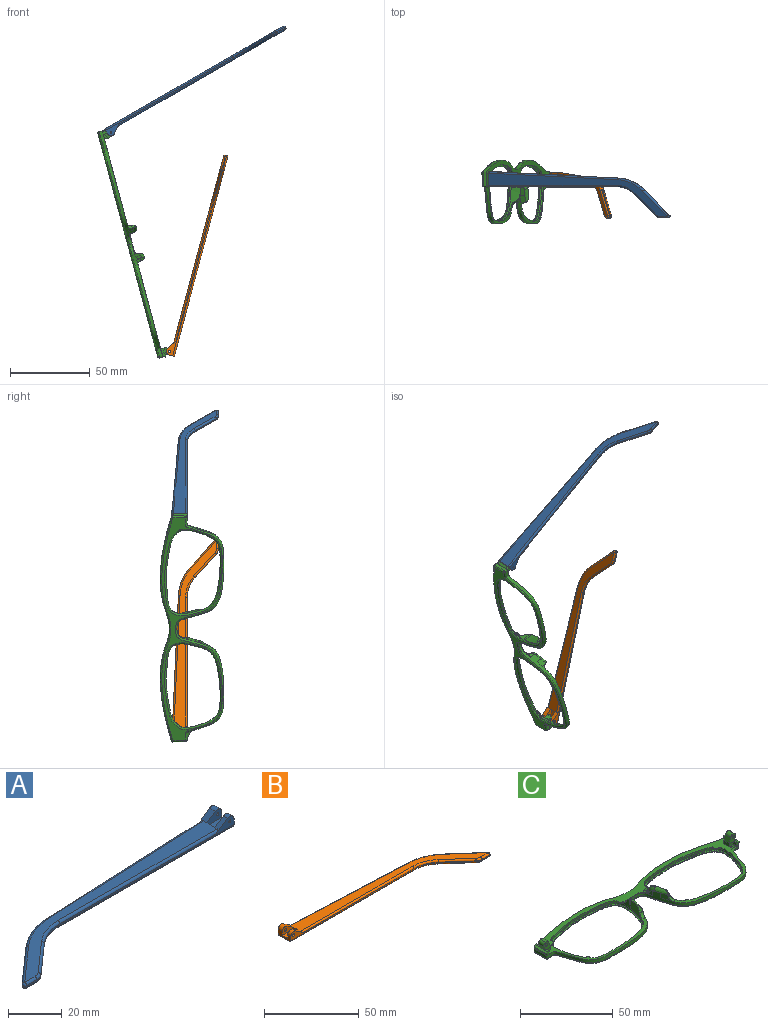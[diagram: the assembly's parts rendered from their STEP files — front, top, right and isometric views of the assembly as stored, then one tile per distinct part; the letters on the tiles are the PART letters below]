
ASSEMBLY  parts=3 mates=2
PART A: 43 faces, bbox 130.2x29.5x5.9 mm
  f0: plane 9.62x3.72mm, normal (1,0,0), area 24.7mm2, adj f1,f3,f4,f5,f10,f16,f18,f28
  f1: cylinder r=2.2mm len=3.45mm, axis (0,-1,0), area 11mm2, adj f0,f2,f4,f37
  f2: plane 6.01x3.91mm, normal (-0.55,0,0.84), area 12.7mm2, adj f1,f4,f9,f19,f37
  f3: plane 2.26x0.1mm, normal (0,0,1), area 0.1mm2, adj f0,f5,f18
  f4: plane 92.1x4.9mm, normal (0,-1,0), area 79.9mm2, adj f0,f1,f2,f14,f19,f36,f42
  f5: plane 93.42x4.13mm, normal (-0.04,1,0), area 64.8mm2, adj f0,f3,f11,f15,f17,f27,f28
  f6: plane 17.82x15.72mm, normal (-0.66,0.75,0), area 14.3mm2, adj f11,f12,f25,f30
  f7: plane 5.46x0.6mm, normal (0,-1,0), area 3.3mm2, adj f12,f13,f23,f32
  f8: plane 14.99x13.23mm, normal (0.66,-0.75,0), area 12mm2, adj f13,f14,f21,f34
  f9: plane 121.18x26.73mm, normal (0,0,1), area 627.7mm2, adj f2,f17,f19,f20,f21,f22,f23,f25
  f10: plane 129.1x27.08mm, normal (0,0,-1), area 686.5mm2, adj f0,f28,f29,f30,f32,f33,f34,f35
  f11: cylinder r=30mm len=18.52mm, axis (0,0,-1), area 12.2mm2, adj f5,f6,f26,f29
  f12: cylinder r=1mm len=1.75mm, axis (0,0,-1), area 1.5mm2, adj f6,f7,f24,f31
  f13: cylinder r=5mm len=3.31mm, axis (0,0,-1), area 2.2mm2, adj f7,f8,f22,f33
  f14: cylinder r=20mm len=13.23mm, axis (0,0,1), area 8.7mm2, adj f4,f8,f20,f35
  f15: plane 5.66x0.25mm, normal (0,0,-1), area 0.7mm2, adj f5,f17,f18
  f16: cylinder r=2.2mm len=3.45mm, axis (0,-1,0), area 14.8mm2, adj f0,f17,f18,f38
  f17: plane 6.01x3.91mm, normal (-0.55,0,0.84), area 16.9mm2, adj f5,f9,f15,f16,f18,f27,f38
  f18: plane 7.92x3.3mm, normal (0,1,0), area 15.9mm2, adj f0,f3,f15,f16,f17,f41
  f19: cylinder r=1mm len=84.18mm, axis (-1,0,0), area 131.4mm2, adj f2,f4,f9,f20
  f20: torus R=21mm, axis (0,0,1), area 23.1mm2, adj f9,f14,f19,f21
  f21: cylinder r=1mm len=15.65mm, axis (-0.75,-0.66,0), area 31.4mm2, adj f8,f9,f20,f22
  f22: torus R=4mm, axis (0,0,1), area 5.3mm2, adj f9,f13,f21,f23
  f23: cylinder r=1mm len=5.46mm, axis (-1,0,0), area 8.6mm2, adj f7,f9,f22,f24
  f24: sphere r=1mm, area 2.4mm2, adj f12,f23,f25
  f25: cylinder r=1mm len=18.48mm, axis (0.75,0.66,0), area 37.3mm2, adj f6,f9,f24,f26
  f26: torus R=29mm, axis (0,0,1), area 31.6mm2, adj f9,f11,f25,f27
  f27: cylinder r=1mm len=85.5mm, axis (1,0.04,0), area 133.5mm2, adj f5,f9,f17,f26
  f28: cylinder r=1mm len=93.46mm, axis (-1,-0.04,0), area 146.9mm2, adj f0,f5,f10,f29
  f29: torus R=29mm, axis (0,0,1), area 31.6mm2, adj f10,f11,f28,f30
  f30: cylinder r=1mm len=18.48mm, axis (-0.75,-0.66,0), area 37.3mm2, adj f6,f10,f29,f31
  f31: sphere r=1mm, area 2.4mm2, adj f12,f30,f32
  f32: cylinder r=1mm len=5.46mm, axis (1,0,0), area 8.6mm2, adj f7,f10,f31,f33
  f33: torus R=4mm, axis (0,0,1), area 5.3mm2, adj f10,f13,f32,f34
  f34: cylinder r=1mm len=15.65mm, axis (0.75,0.66,0), area 31.4mm2, adj f8,f10,f33,f35
  f35: torus R=21mm, axis (0,0,1), area 23.1mm2, adj f10,f14,f34,f36
  f36: cylinder r=1mm len=92.1mm, axis (1,0,0), area 144.7mm2, adj f0,f4,f10,f35
  f37: plane 7.92x4.7mm, normal (0,1,0), area 27mm2, adj f0,f1,f2,f39,f40,f42
  f38: plane 7.92x4.7mm, normal (0,-1,0), area 27mm2, adj f0,f16,f17,f39,f40,f41
  f39: plane 7.92x4.1mm, normal (0,0,1), area 32.5mm2, adj f0,f37,f38,f40
  f40: plane 4.1x1.4mm, normal (1,0,0), area 5.7mm2, adj f9,f37,f38,f39
  f41: cylinder r=0.5mm len=3.1mm, axis (0,-1,0), area 9.7mm2, adj f18,f38
  f42: cylinder r=0.5mm len=2.3mm, axis (0,-1,0), area 7.2mm2, adj f4,f37
PART B: 43 faces, bbox 130.2x29.5x5.9 mm
  f0: plane 9.62x3.72mm, normal (-1,0,0), area 24.7mm2, adj f1,f3,f4,f5,f10,f16,f18,f28
  f1: cylinder r=2.2mm len=3.45mm, axis (0,-1,0), area 11mm2, adj f0,f2,f4,f37
  f2: plane 6.01x3.91mm, normal (0.55,0,0.84), area 12.7mm2, adj f1,f4,f9,f19,f37
  f3: plane 2.26x0.1mm, normal (0,0,1), area 0.1mm2, adj f0,f5,f18
  f4: plane 92.1x4.9mm, normal (0,-1,0), area 78.2mm2, adj f0,f1,f2,f14,f19,f36,f42
  f5: plane 93.42x4.13mm, normal (0.04,1,0), area 64.8mm2, adj f0,f3,f11,f15,f17,f27,f28
  f6: plane 17.82x15.72mm, normal (0.66,0.75,0), area 14.3mm2, adj f11,f12,f25,f30
  f7: plane 5.46x0.6mm, normal (0,-1,0), area 3.3mm2, adj f12,f13,f23,f32
  f8: plane 14.99x13.23mm, normal (-0.66,-0.75,0), area 12mm2, adj f13,f14,f21,f34
  f9: plane 121.18x26.73mm, normal (0,0,1), area 627.7mm2, adj f2,f17,f19,f20,f21,f22,f23,f25
  f10: plane 129.1x27.08mm, normal (0,0,-1), area 686.5mm2, adj f0,f28,f29,f30,f32,f33,f34,f35
  f11: cylinder r=30mm len=18.52mm, axis (0,0,-1), area 12.2mm2, adj f5,f6,f26,f29
  f12: cylinder r=1mm len=1.75mm, axis (0,0,-1), area 1.5mm2, adj f6,f7,f24,f31
  f13: cylinder r=5mm len=3.31mm, axis (0,0,-1), area 2.2mm2, adj f7,f8,f22,f33
  f14: cylinder r=20mm len=13.23mm, axis (0,0,1), area 8.7mm2, adj f4,f8,f20,f35
  f15: plane 5.66x0.25mm, normal (0,0,-1), area 0.7mm2, adj f5,f17,f18
  f16: cylinder r=2.2mm len=3.45mm, axis (0,-1,0), area 14.8mm2, adj f0,f17,f18,f38
  f17: plane 6.01x3.91mm, normal (0.55,0,0.84), area 16.9mm2, adj f5,f9,f15,f16,f18,f27,f38
  f18: plane 7.92x3.3mm, normal (0,1,0), area 14.3mm2, adj f0,f3,f15,f16,f17,f41
  f19: cylinder r=1mm len=84.18mm, axis (1,0,0), area 131.4mm2, adj f2,f4,f9,f20
  f20: torus R=21mm, axis (0,0,1), area 23.1mm2, adj f9,f14,f19,f21
  f21: cylinder r=1mm len=15.65mm, axis (0.75,-0.66,0), area 31.4mm2, adj f8,f9,f20,f22
  f22: torus R=4mm, axis (0,0,1), area 5.3mm2, adj f9,f13,f21,f23
  f23: cylinder r=1mm len=5.46mm, axis (1,0,0), area 8.6mm2, adj f7,f9,f22,f24
  f24: sphere r=1mm, area 2.4mm2, adj f12,f23,f25
  f25: cylinder r=1mm len=18.48mm, axis (-0.75,0.66,0), area 37.3mm2, adj f6,f9,f24,f26
  f26: torus R=29mm, axis (0,0,1), area 31.6mm2, adj f9,f11,f25,f27
  f27: cylinder r=1mm len=85.5mm, axis (-1,0.04,0), area 133.5mm2, adj f5,f9,f17,f26
  f28: cylinder r=1mm len=93.46mm, axis (1,-0.04,0), area 146.9mm2, adj f0,f5,f10,f29
  f29: torus R=29mm, axis (0,0,1), area 31.6mm2, adj f10,f11,f28,f30
  f30: cylinder r=1mm len=18.48mm, axis (0.75,-0.66,0), area 37.3mm2, adj f6,f10,f29,f31
  f31: sphere r=1mm, area 2.4mm2, adj f12,f30,f32
  f32: cylinder r=1mm len=5.46mm, axis (-1,0,0), area 8.6mm2, adj f7,f10,f31,f33
  f33: torus R=4mm, axis (0,0,1), area 5.3mm2, adj f10,f13,f32,f34
  f34: cylinder r=1mm len=15.65mm, axis (-0.75,0.66,0), area 31.4mm2, adj f8,f10,f33,f35
  f35: torus R=21mm, axis (0,0,1), area 23.1mm2, adj f10,f14,f34,f36
  f36: cylinder r=1mm len=92.1mm, axis (-1,0,0), area 144.7mm2, adj f0,f4,f10,f35
  f37: plane 7.92x4.7mm, normal (0,1,0), area 25.4mm2, adj f0,f1,f2,f39,f40,f42
  f38: plane 7.92x4.7mm, normal (0,-1,0), area 25.4mm2, adj f0,f16,f17,f39,f40,f41
  f39: plane 7.92x4.1mm, normal (0,0,1), area 32.5mm2, adj f0,f37,f38,f40
  f40: plane 4.1x1.4mm, normal (-1,0,0), area 5.7mm2, adj f9,f37,f38,f39
  f41: cylinder r=0.88mm len=3.1mm, axis (0,-1,0), area 17mm2, adj f18,f38
  f42: cylinder r=0.88mm len=2.3mm, axis (0,-1,0), area 12.6mm2, adj f4,f37
PART C: 118 faces, bbox 148.1x40.9x17.9 mm
  f0: bspline ~1.82x1.22mm, area 0.7mm2, adj f2,f7,f37,f52
  f1: plane 147.69x40.46mm, normal (0,0,1), area 858.2mm2, adj f4,f5,f6,f7,f8,f12,f20,f23
  f2: bspline ~6.1x4.93mm, area 12.7mm2, adj f0,f7,f37,f41,f43,f52,f53
  f3: plane 4.46x1.45mm, normal (0,0,1), area 0.1mm2, adj f7,f38
  f4: plane 1.23x0.04mm, normal (0,0,1), area 0mm2, adj f1,f7,f22
  f5: plane 6.97x5.07mm, normal (0,1,0), area 22.7mm2, adj f1,f20,f21,f25,f27,f28,f30,f31
  f6: plane 3.2x2.36mm, normal (0,-1,0), area 5.7mm2, adj f1,f20,f26,f29
  f7: extruded ~73.26x39.84mm, area 292.7mm2, adj f0,f1,f2,f3,f4,f8,f13,f14
  f8: extruded ~35.39x5.69mm, area 72.2mm2, adj f1,f7,f18,f67
  f9: plane 144.78x37.85mm, normal (0,0,-1), area 582.4mm2, adj f13,f15,f17,f18,f19,f71,f73,f75
  f10: plane 56.06x35.45mm, normal (0,0,1), area 127mm2, adj f11,f19
  f11: extruded ~55.69x35.36mm, area 160.5mm2, adj f10,f12
  f12: extruded ~55.69x35.36mm, area 226.3mm2, adj f1,f11,f39,f40,f41,f42,f43,f44
  f13: bspline ~73.27x30.39mm, area 161.7mm2, adj f7,f9,f14,f71
  f14: bspline ~1x1mm, area 0.8mm2, adj f7,f13,f15
  f15: bspline ~8.99x1.23mm, area 12.6mm2, adj f7,f9,f14,f16
  f16: bspline ~1.04x1mm, area 0.7mm2, adj f7,f15,f17
  f17: bspline ~45.86x8.59mm, area 59.8mm2, adj f7,f9,f16,f18
  f18: bspline ~37.01x6.7mm, area 56.6mm2, adj f8,f9,f17,f76
  f19: bspline ~56.23x35.9mm, area 235.3mm2, adj f9,f10
  f20: plane 4x2.36mm, normal (-1,0,0), area 9.5mm2, adj f1,f5,f6,f21
  f21: plane 4x0.02mm, normal (0.34,0,0.94), area 0.1mm2, adj f5,f20,f28
  f22: plane 2.76x2.53mm, normal (0,-1,0), area 3.9mm2, adj f4,f26,f27,f35,f56
  f23: plane 7.67x1.6mm, normal (0.94,0,-0.34), area 13mm2, adj f1,f35,f36,f56
  f24: plane 2.1x1.69mm, normal (0,1,0), area 2.8mm2, adj f1,f25,f27,f36,f56
  f25: plane 3.3x2.1mm, normal (-1,0,0), area 6.9mm2, adj f1,f5,f24,f27
  f26: plane 2.35x2.1mm, normal (-1,0,0), area 4.9mm2, adj f1,f6,f22,f27,f29
  f27: plane 9.65x1.24mm, normal (0,0,1), area 8.2mm2, adj f5,f22,f24,f25,f26,f29,f30,f56
  f28: plane 4x3.31mm, normal (-0.94,0,0.34), area 14.1mm2, adj f5,f21,f29,f32
  f29: plane 5.77x5.06mm, normal (0,-1,0), area 17mm2, adj f6,f26,f27,f28,f30,f31,f32,f33
  f30: plane 4x2.21mm, normal (0.94,0,-0.34), area 9.4mm2, adj f5,f27,f29,f33
  f31: plane 4x0.01mm, normal (0.34,0,0.94), area 0mm2, adj f5,f29,f32,f33
  f32: cylinder r=1.98mm len=4mm, axis (0,1,0), area 12.4mm2, adj f5,f28,f29,f31
  f33: cylinder r=1.98mm len=4mm, axis (0,-1,0), area 12.4mm2, adj f5,f29,f30,f31
  f34: cylinder r=0.88mm len=4mm, axis (0,-1,0), area 22mm2, adj f5,f29
  f35: cone r=1mm half-angle=20deg, axis (0,0,1), area 2.3mm2, adj f1,f22,f23,f56
  f36: cylinder r=1mm len=2.28mm, axis (-0.34,0,-0.94), area 3mm2, adj f1,f23,f24,f56
  f37: extruded ~3.67x3.11mm, area 5.9mm2, adj f0,f2,f7,f59
  f38: extruded ~4.44x3.32mm, area 15.1mm2, adj f3,f7,f42,f43,f55
  f39: extruded ~4.98x1.37mm, area 6.6mm2, adj f12,f41
  f40: plane 3.63x0.97mm, normal (0,0,1), area 0.3mm2, adj f12,f41,f43
  f41: bspline ~15.5x15.35mm, area 6.4mm2, adj f2,f12,f39,f40,f54
  f42: bspline ~7.26x7.26mm, area 6.3mm2, adj f12,f38,f43,f55
  f43: bspline ~10.29x4.84mm, area 21.4mm2, adj f2,f7,f12,f38,f40,f42
  f44: plane 3.19x1.37mm, normal (0,0,-1), area 2.1mm2, adj f12,f45
  f45: cylinder r=2.28mm len=3.17mm, axis (0,0,1), area 2.1mm2, adj f1,f12,f44,f54
  f46: plane 3.14x2.79mm, normal (0,0,-1), area 3.9mm2, adj f12,f47
  f47: cylinder r=2.28mm len=3.13mm, axis (0,0,1), area 2.5mm2, adj f1,f12,f46
  f48: plane 1.79x1.31mm, normal (0,0,-1), area 0.9mm2, adj f12,f49
  f49: cylinder r=1.3mm len=1.78mm, axis (0,0,1), area 1.3mm2, adj f1,f12,f48
  f50: plane 1.95x1.68mm, normal (0,0,-1), area 1.5mm2, adj f12,f51
  f51: cylinder r=1.3mm len=1.93mm, axis (0,0,1), area 1.5mm2, adj f1,f12,f50
  f52: bspline ~2.66x2.04mm, area 1.9mm2, adj f0,f2,f7,f53,f58
  f53: bspline ~3.55x3.47mm, area 3.7mm2, adj f1,f2,f52,f54,f58
  f54: bspline ~6.16x4.45mm, area 7.9mm2, adj f1,f12,f41,f45,f53
  f55: bspline ~3.7x3.66mm, area 7.8mm2, adj f1,f7,f12,f38,f42
  f56: plane 9.71x1.44mm, normal (0.34,0,0.94), area 13.9mm2, adj f22,f23,f24,f27,f35,f36
  f57: bspline ~6.38x2.14mm, area 2.6mm2, adj f1,f7,f58,f115
  f58: bspline ~2.1x1.46mm, area 0.6mm2, adj f7,f52,f53,f57
  f59: bspline ~5.24x1.75mm, area 0mm2, adj f7,f37
  f60: bspline ~2.19x1.4mm, area 0.7mm2, adj f61,f66,f95,f110
  f61: bspline ~6.1x4.93mm, area 12.6mm2, adj f60,f66,f95,f99,f101,f110,f111
  f62: plane 4.46x1.45mm, normal (0,0,1), area 0.1mm2, adj f66,f96
  f63: plane 1.23x0.04mm, normal (0,0,1), area 0mm2, adj f1,f66,f80
  f64: plane 6.97x5.07mm, normal (0,1,0), area 22.7mm2, adj f1,f78,f79,f83,f85,f86,f88,f89
  f65: plane 3.2x2.36mm, normal (0,-1,0), area 5.7mm2, adj f1,f78,f84,f87
  f66: extruded ~73.26x39.84mm, area 292.7mm2, adj f1,f7,f60,f61,f62,f63,f67,f71
  f67: extruded ~35.39x5.69mm, area 72.2mm2, adj f1,f8,f66,f76
  f68: plane 56.06x35.45mm, normal (0,0,1), area 127mm2, adj f69,f77
  f69: extruded ~55.69x35.36mm, area 160.5mm2, adj f68,f70
  f70: extruded ~55.69x35.36mm, area 226.4mm2, adj f1,f69,f97,f98,f99,f100,f101,f102
  f71: bspline ~73.83x30.39mm, area 161.7mm2, adj f9,f13,f66,f72
  f72: bspline ~1x1mm, area 0.8mm2, adj f66,f71,f73
  f73: bspline ~8.99x1.23mm, area 12.6mm2, adj f9,f66,f72,f74
  f74: bspline ~1.04x1mm, area 0.8mm2, adj f66,f73,f75
  f75: bspline ~45.86x8.59mm, area 59.8mm2, adj f9,f66,f74,f76
  f76: bspline ~37.01x6.7mm, area 56.6mm2, adj f9,f18,f67,f75
  f77: bspline ~56.22x35.9mm, area 235.3mm2, adj f9,f68
  f78: plane 4x2.36mm, normal (1,0,0), area 9.5mm2, adj f1,f64,f65,f79
  f79: plane 4x0.02mm, normal (-0.34,0,0.94), area 0.1mm2, adj f64,f78,f86
  f80: plane 2.76x2.53mm, normal (0,-1,0), area 3.9mm2, adj f63,f84,f85,f93,f114
  f81: plane 7.67x1.6mm, normal (-0.94,0,-0.34), area 13mm2, adj f1,f93,f94,f114
  f82: plane 2.1x1.69mm, normal (0,1,0), area 2.8mm2, adj f1,f83,f85,f94,f114
  f83: plane 3.3x2.1mm, normal (1,0,0), area 6.9mm2, adj f1,f64,f82,f85
  f84: plane 2.35x2.1mm, normal (1,0,0), area 4.9mm2, adj f1,f65,f80,f85,f87
  f85: plane 9.65x1.24mm, normal (0,0,1), area 8.2mm2, adj f64,f80,f82,f83,f84,f87,f88,f114
  f86: plane 4x3.31mm, normal (0.94,0,0.34), area 14.1mm2, adj f64,f79,f87,f90
  f87: plane 5.77x5.06mm, normal (0,-1,0), area 17mm2, adj f65,f84,f85,f86,f88,f89,f90,f91
  f88: plane 4x2.21mm, normal (-0.94,0,-0.34), area 9.4mm2, adj f64,f85,f87,f91
  f89: plane 4x0.01mm, normal (-0.34,0,0.94), area 0mm2, adj f64,f87,f90,f91
  f90: cylinder r=1.98mm len=4mm, axis (0,1,0), area 12.4mm2, adj f64,f86,f87,f89
  f91: cylinder r=1.98mm len=4mm, axis (0,-1,0), area 12.4mm2, adj f64,f87,f88,f89
  f92: cylinder r=0.88mm len=4mm, axis (0,-1,0), area 22mm2, adj f64,f87
  f93: cone r=1mm half-angle=20deg, axis (0,0,1), area 2.3mm2, adj f1,f80,f81,f114
  f94: cylinder r=1mm len=2.28mm, axis (0.34,0,-0.94), area 3mm2, adj f1,f81,f82,f114
  f95: extruded ~3.67x3.11mm, area 5.9mm2, adj f60,f61,f66,f117
  f96: extruded ~4.44x3.32mm, area 15.1mm2, adj f62,f66,f100,f101,f113
  f97: extruded ~4.98x1.36mm, area 6.6mm2, adj f70,f99
  f98: plane 3.63x0.97mm, normal (0,0,1), area 0.3mm2, adj f70,f99,f101
  f99: bspline ~15.5x15.35mm, area 6.4mm2, adj f61,f70,f97,f98,f112
  f100: bspline ~7.26x7.26mm, area 6.2mm2, adj f70,f96,f101,f113
  f101: bspline ~10.29x4.84mm, area 21.5mm2, adj f61,f66,f70,f96,f98,f100
  f102: plane 3.19x1.37mm, normal (0,0,-1), area 2.1mm2, adj f70,f103
  f103: cylinder r=2.28mm len=3.17mm, axis (0,0,1), area 2.1mm2, adj f1,f70,f102,f112
  f104: plane 3.14x2.79mm, normal (0,0,-1), area 3.9mm2, adj f70,f105
  f105: cylinder r=2.28mm len=3.13mm, axis (0,0,1), area 2.5mm2, adj f1,f70,f104
  f106: plane 1.79x1.31mm, normal (0,0,-1), area 0.9mm2, adj f70,f107
  f107: cylinder r=1.3mm len=1.78mm, axis (0,0,1), area 1.3mm2, adj f1,f70,f106
  f108: plane 1.95x1.68mm, normal (0,0,-1), area 1.5mm2, adj f70,f109
  f109: cylinder r=1.3mm len=1.93mm, axis (0,0,1), area 1.5mm2, adj f1,f70,f108
  f110: bspline ~2.65x2.03mm, area 1.9mm2, adj f60,f61,f66,f111,f116
  f111: bspline ~3.55x3.47mm, area 3.7mm2, adj f1,f61,f110,f112,f116
  f112: bspline ~5.94x4.42mm, area 7.9mm2, adj f1,f70,f99,f103,f111
  f113: bspline ~3.7x3.66mm, area 7.8mm2, adj f1,f66,f70,f96,f100
  f114: plane 9.71x1.44mm, normal (-0.34,0,0.94), area 13.9mm2, adj f80,f81,f82,f85,f93,f94
  f115: bspline ~6.38x2.14mm, area 2.6mm2, adj f1,f57,f66,f116
  f116: bspline ~2.1x1.46mm, area 0.6mm2, adj f66,f110,f111,f115
  f117: bspline ~5.24x1.75mm, area 0mm2, adj f66,f95
PLACE A rot(axis=(0,1,0),150deg) t=(-72.65,21.06,69.08)mm
PLACE B rot(axis=(0,-1,0),75deg) t=(-98.69,21.06,-164.02)mm
PLACE C rot(axis=(0,1,0),75deg) t=(-110.82,25.67,-34.37)mm
MATE revolute A.f1 <-> C.f90  axis (0,-1,0) through (-122.46,29.52,36.05)mm
MATE revolute B.f41 <-> C.f33  axis (0,-1,0) through (-85.68,29.52,-101.2)mm
